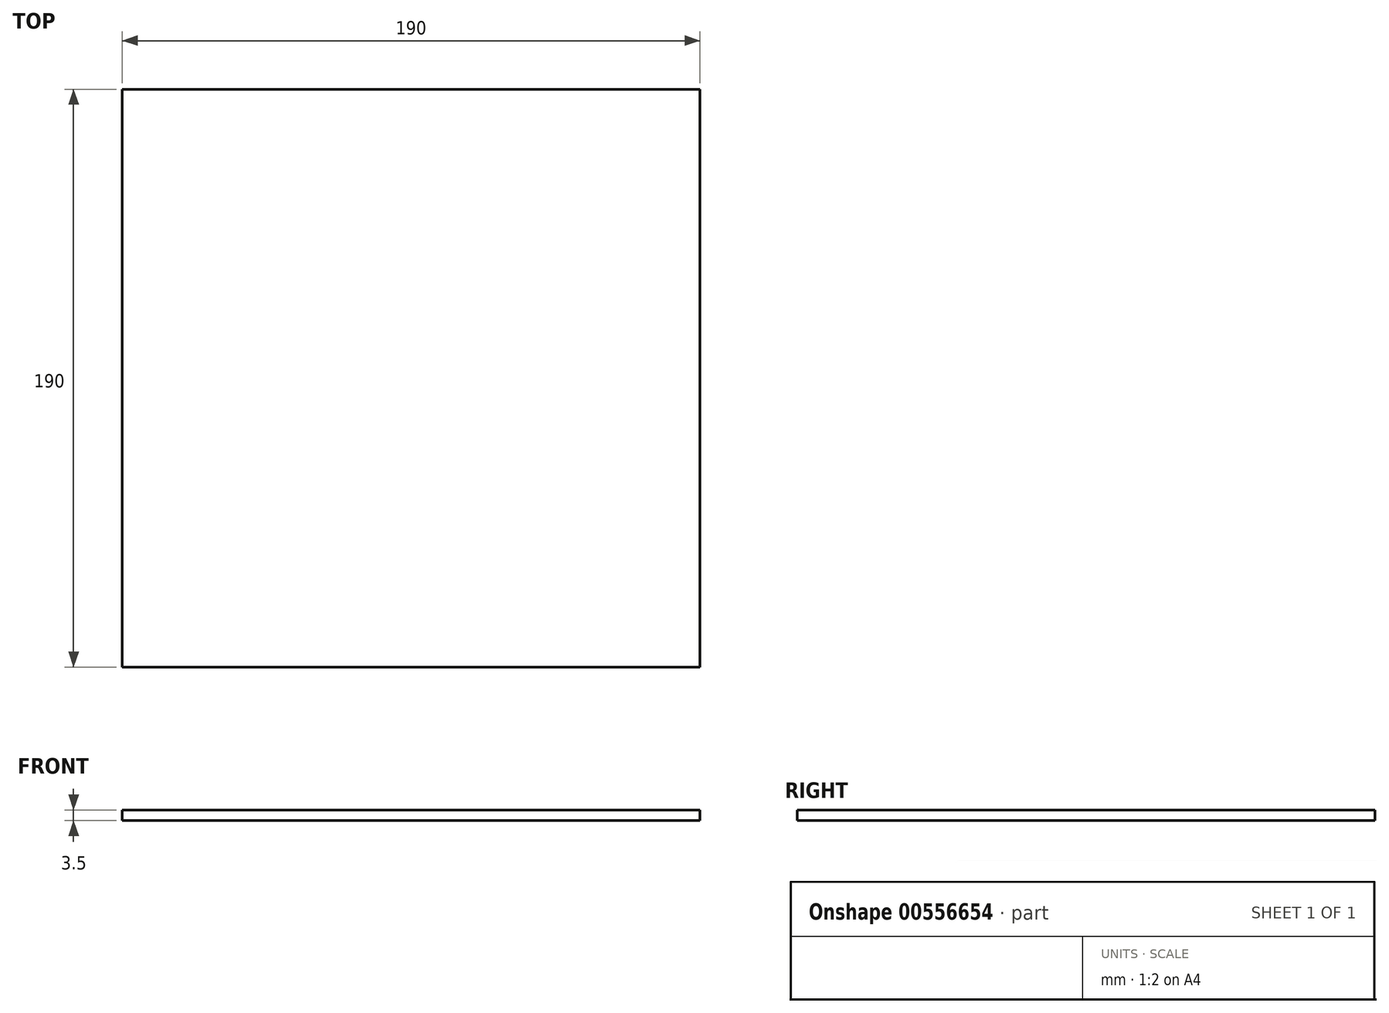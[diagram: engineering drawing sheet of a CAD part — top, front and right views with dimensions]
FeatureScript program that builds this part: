
annotation { "Feature Type Name" : "Feature", "Feature Type Description" : "" }
export const myFeature = defineFeature(function(context is Context, id is Id, definition is map)
    precondition{}
    {
        {
            var Q0;
            Q0=qCreatedBy(makeId("Top.planeOp"),FACE);
            var sketch = newSketch(context, id + "F0", { "sketchPlane" : qUnion([Q0])});
            skLineSegment(sketch, "E0", {"start": v(0, 0) * mm, "end": v(0, 190) * mm});
            skLineSegment(sketch, "E1", {"start": v(0, 190) * mm, "end": v(190, 190) * mm});
            skLineSegment(sketch, "E2", {"start": v(190, 190) * mm, "end": v(190, 0) * mm});
            skLineSegment(sketch, "E3", {"start": v(190, 0) * mm, "end": v(0, 0) * mm});
            skSolve(sketch);
        }
        {
            var Q0;
            Q0 = qSketchRegion(id + "F0", true);
            extrude(context, id + "F1", {"entities" : qUnion([Q0]), "depth" : 2 * mm, "offsetDistance" : 25 * mm});
        }
        {
            var Q0;
            Q0 = qSketchRegion(id + "F0", true);
            extrude(context, id + "F2", {"entities" : qUnion([Q0]), "operationType" : NewBodyOperationType.ADD, "endBound" : BoundingType.SYMMETRIC, "depth" : 3 * mm, "offsetDistance" : 25 * mm});
        }
    });
